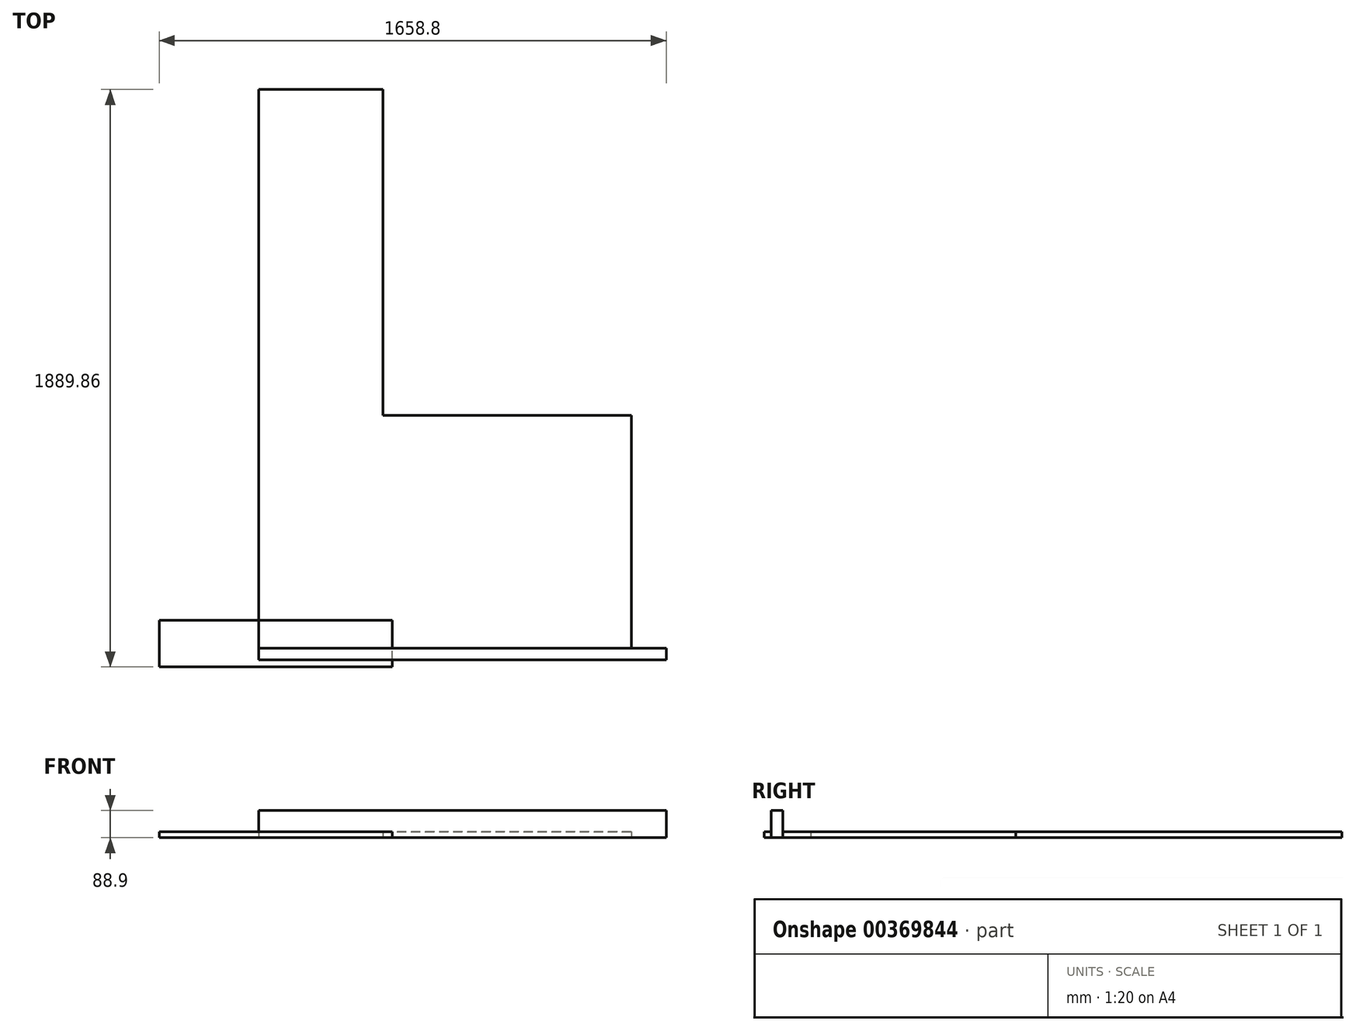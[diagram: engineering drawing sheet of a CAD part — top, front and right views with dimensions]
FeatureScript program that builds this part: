
annotation { "Feature Type Name" : "Feature", "Feature Type Description" : "" }
export const myFeature = defineFeature(function(context is Context, id is Id, definition is map)
    precondition{}
    {
        {
            var Q0;
            Q0=qCreatedBy(makeId("Top.planeOp"),FACE);
            var sketch = newSketch(context, id + "F0", { "sketchPlane" : qUnion([Q0])});
            skLineSegment(sketch, "E0.bottom", {"start": v(0, 0) * mm, "end": v(1333.5, 0) * mm});
            skLineSegment(sketch, "E0.top", {"start": v(0, -38.1) * mm, "end": v(1333.5, -38.1) * mm});
            skLineSegment(sketch, "E0.left", {"start": v(0, 0) * mm, "end": v(0, -38.1) * mm});
            skLineSegment(sketch, "E0.right", {"start": v(1333.5, 0) * mm, "end": v(1333.5, -38.1) * mm});
            skSolve(sketch);
        }
        {
            var Q0;
            Q0=qSketchRegion(id+"F0",true);
            extrude(context, id + "F1", {"entities" : qUnion([Q0]), "depth" : 88.9 * mm});
        }
        {
            var Q0;
            Q0=qCreatedBy(makeId("Top.planeOp"),FACE);
            var sketch = newSketch(context, id + "F2", { "sketchPlane" : qUnion([Q0])});
            skLineSegment(sketch, "E1", {"start": v(0, 0) * mm, "end": v(0, 1828.8) * mm});
            skLineSegment(sketch, "E2", {"start": v(0, 1828.8) * mm, "end": v(406.4, 1828.8) * mm});
            skLineSegment(sketch, "E3", {"start": v(406.4, 1828.8) * mm, "end": v(406.4, 762) * mm});
            skLineSegment(sketch, "E4", {"start": v(406.4, 762) * mm, "end": v(1219.2, 762) * mm});
            skLineSegment(sketch, "E5", {"start": v(1219.2, 762) * mm, "end": v(1219.2, 0) * mm});
            skLineSegment(sketch, "E6", {"start": v(1219.2, 0) * mm, "end": v(0, 0) * mm});
            skSolve(sketch);
        }
        {
            var Q0;
            Q0=makeQuery(id+"F2.imprint","IMPRINT",FACE,{"disambiguationData":[TD([[makeQuery(id+"F2.imprint","IMPRINT",EDGE,{"derivedFrom":sQuery(id+"F2.wireOp",EDGE,"E1")}),-1.0]])]});
            extrude(context, id + "F3", {"entities" : qUnion([Q0]), "depth" : 19.05 * mm});
        }
        {
            var Q0;
            Q0=qCreatedBy(makeId("Top.planeOp"),FACE);
            var sketch = newSketch(context, id + "F4", { "sketchPlane" : qUnion([Q0])});
            skLineSegment(sketch, "E7.bottom", {"start": v(436.7, -61.06) * mm, "end": v(-325.3, -61.06) * mm});
            skLineSegment(sketch, "E7.top", {"start": v(436.7, 91.34) * mm, "end": v(-325.3, 91.34) * mm});
            skLineSegment(sketch, "E7.left", {"start": v(436.7, -61.06) * mm, "end": v(436.7, 91.34) * mm});
            skLineSegment(sketch, "E7.right", {"start": v(-325.3, -61.06) * mm, "end": v(-325.3, 91.34) * mm});
            skSolve(sketch);
        }
        {
            var Q0;
            Q0=makeQuery(id+"F4.imprint","IMPRINT",FACE,{"disambiguationData":[TD([[makeQuery(id+"F4.imprint","IMPRINT",EDGE,{"derivedFrom":sQuery(id+"F4.wireOp",EDGE,"E7.bottom")}),-1.0]])]});
            extrude(context, id + "F5", {"entities" : qUnion([Q0]), "depth" : 19.05 * mm});
        }
    });
